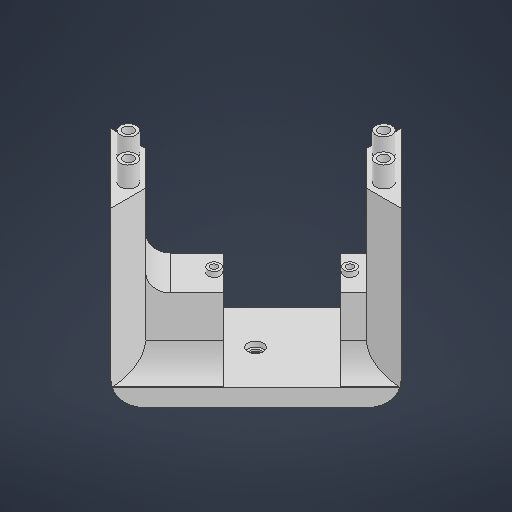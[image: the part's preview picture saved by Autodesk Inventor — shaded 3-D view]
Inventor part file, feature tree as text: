
AUTODESK INVENTOR PART (.ipt)
format: ipt  version: 2025.1 (Build 291241000, 241)  size: 641,024 bytes
history: native  units: in
note: dims shown in document units (in); Inventor stores cm internally (conversion verified against a paired STEP export)
features: sketch x14, extrude x14, projected_geometry x4, plane x3, fillet x3
ambient origin geometry x8: Origin, YZ Plane, XZ Plane, XY Plane, X Axis, Y Axis, Z Axis, Center Point
bodies: Solid1 (feature_tree)
feature tree (38):
  sketch  "Sketch1"  dims[d0=0.185in d1=0.1969in d2=0.1969in d3=0.185in d4=0.185in d5=0.185in d6=0.1969in d7=0.1969in d8=0.2362in d9=0.0in]
  extrude  "Extrusion1"  Depth=0.2362in TaperAngle=0.0deg
  extrude  "Extrusion2"  Depth=0.1969in TaperAngle=0.0deg
  extrude  "Extrusion3"  Depth=0.6299in
  sketch  "Sketch3"  dims[d16=45.0deg d17=0.1575in]
  plane  "Work Plane3"
  extrude  "Extrusion5"  Depth=0.1575in
  extrude  "Extrusion6"  Depth=0.6299in
  sketch  "Sketch6"  dims[d26=0.1181in d27=0.1181in]
  plane  "Work Plane1"
  extrude  "Extrusion7"  Depth=0.1181in
  fillet  "Fillet6"  Radius=0.1181in
  sketch  "Sketch8"  dims[d35=-0.9557in d36=0.189in d37=0.3346in]
  extrude  "Extrusion8"  Depth=0.1181in
  extrude  "Extrusion9"  Depth=0.1181in
  fillet  "Fillet7"  Radius=0.315in
  plane  "Work Plane2"
  extrude  "Extrusion10"  Depth=0.189in
  fillet  "Fillet8"  Radius=0.3346in
  extrude  "Extrusion11"  TaperAngle=45.0deg  [1 undecoded]
  extrude  "Extrusion12"  Depth=0.1024in
  extrude  "Extrusion13"  TaperAngle=135.0deg  [1 undecoded]
  extrude  "Extrusion14"  Depth=0.6811in
  extrude  "Extrusion15"  Depth=0.2662in
  sketch  "Sketch2"  dims[d14=0.5118in d15=0.6299in]
  sketch  "Sketch4"  dims[d18=90.0deg d19=0.6299in]
  sketch  "Sketch5"  dims[d20=0.1575in d23=0.1772in d24=0.1181in d25=0.0in]
  projected_geometry  "Projected Loop1"
  projected_geometry  "Projected Loop2"
  sketch  "Sketch7"  dims[d28=0.1181in d29=0.1181in d30=0.315in d31=0.0in]
  sketch  "Sketch9"  dims[d38=0.7598in d39=45.0deg]
  sketch  "Sketch10"  dims[d40=0.1024in d41=0.1024in]
  sketch  "Sketch11"  dims[d42=0.2559in d43=135.0deg]
  sketch  "Sketch Circular Pattern1"  dims[d10=1.6929in d11=0.0in d12=0.1969in d13=0.0in]
  sketch  "Sketch12"  dims[d44=135.0deg d45=0.6811in]
  projected_geometry  "Projected Loop3"
  projected_geometry  "Projected Loop4"
  sketch  "Sketch13"  dims[d46=0.2756in d47=0.0in d50=0.2662in d51=0.0787in d52=0.0787in d53=0.1181in d54=0.1909in d55=0.0in d56=0.0591in d57=0.0in d58=0.2662in d59=0.1181in d60=0.0787in d61=0.0in d62=0.2037in d63=0.0787in d64=0.0in d65=0.0787in d66=0.0in d67=0.0669in d68=0.0669in d69=0.6732in d70=0.2087in d71=0.2087in d72=0.4724in d73=0.3465in d74=0.3465in d75=0.1181in d76=0.315in d77=0.7874in d79=45.0deg d81=0.1181in d82=0.0in d83=0.0787in d84=0.3937in d85=0.0in d86=0.1378in d87=0.1378in d88=0.0591in d89=0.0in]
note: 2 required parameter values undecoded (feature->parameter linkage not recoverable at this tier; creation-order binding heuristic only, values carry confidence <= 0.55)
